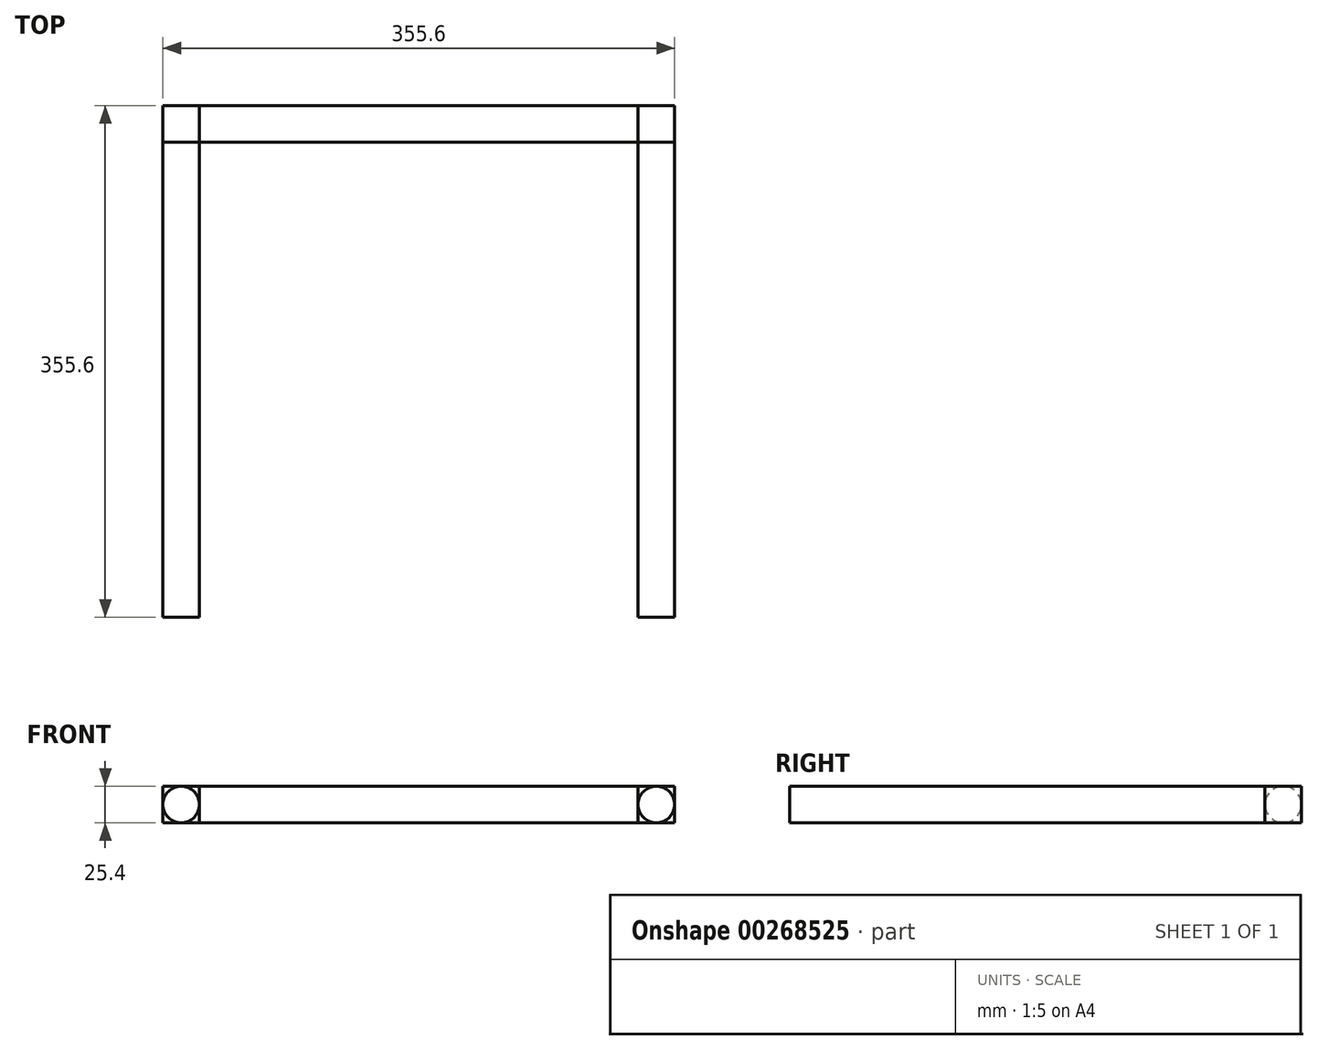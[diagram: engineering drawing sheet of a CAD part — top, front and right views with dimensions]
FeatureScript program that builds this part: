
annotation { "Feature Type Name" : "Feature", "Feature Type Description" : "" }
export const myFeature = defineFeature(function(context is Context, id is Id, definition is map)
    precondition{}
    {
        {
            var Q0;
            Q0=qCreatedBy(makeId("Right.planeOp"),FACE);
            var sketch = newSketch(context, id + "F0", { "sketchPlane" : qUnion([Q0])});
            skCircle(sketch, "E0", {"center": v(0, 0) * mm, "radius": 12.7 * mm});
            skSolve(sketch);
        }
        {
            var Q0;
            Q0 = qSketchRegion(id + "F0", true);
            extrude(context, id + "F1", {"entities" : qUnion([Q0]), "oppositeDirection" : true, "depth" : 152.4 * mm});
        }
        {
            var Q0;
            Q0=makeQuery(id+"F1.opExtrude","CAP_FACE",FACE,{"disambiguationData":[OSD([sQuery(id+"F0.wireOp",EDGE,"E0")])],"isStart":false});
            var sketch = newSketch(context, id + "F2", { "sketchPlane" : qUnion([Q0])});
            skLineSegment(sketch, "E1.bottom", {"start": v(12.7, 12.7) * mm, "end": v(-12.7, 12.7) * mm});
            skLineSegment(sketch, "E1.top", {"start": v(12.7, -12.7) * mm, "end": v(-12.7, -12.7) * mm});
            skLineSegment(sketch, "E1.left", {"start": v(12.7, 12.7) * mm, "end": v(12.7, -12.7) * mm});
            skLineSegment(sketch, "E1.right", {"start": v(-12.7, 12.7) * mm, "end": v(-12.7, -12.7) * mm});
            skPoint(sketch, "E1.middle", {"position": v(0, 0) * mm});
            skSolve(sketch);
        }
        {
            var Q0;
            Q0 = qSketchRegion(id + "F2", true);
            extrude(context, id + "F3", {"entities" : qUnion([Q0]), "operationType" : NewBodyOperationType.ADD, "depth" : 25.4 * mm});
        }
        {
            var Q0;
            Q0=makeQuery(id+"F3.opExtrude","SWEPT_FACE",FACE,{"disambiguationData":[OSD([sQuery(id+"F2.wireOp",EDGE,"E1.left")])]});
            var sketch = newSketch(context, id + "F4", { "sketchPlane" : qUnion([Q0])});
            skCircle(sketch, "E2", {"center": v(-165.1, 0) * mm, "radius": 12.69 * mm});
            skPoint(sketch, "E2.centerSnap0", {"position": v(-165.1, 12.7) * mm});
            skSolve(sketch);
        }
        {
            var Q0;
            Q0 = qSketchRegion(id + "F4", true);
            extrude(context, id + "F5", {"entities" : qUnion([Q0]), "operationType" : NewBodyOperationType.ADD, "depth" : 330.2 * mm});
        }
        {
            var Q0;
            Q0=makeQuery(id+"F1.opExtrude","SWEPT_BODY",BODY,{"disambiguationData":[OSD([sQuery(id+"F0.wireOp",EDGE,"E0")])]});
            var Q1;
            Q1=makeQuery(id+"F1.opExtrude","CAP_FACE",FACE,{"disambiguationData":[OSD([sQuery(id+"F0.wireOp",EDGE,"E0")])],"isStart":true});
            mirror(context, id + "F6", {"operationType" : NewBodyOperationType.ADD, "entities" : qUnion([Q0]), "mirrorPlane" : qUnion([Q1])});
        }
    });
